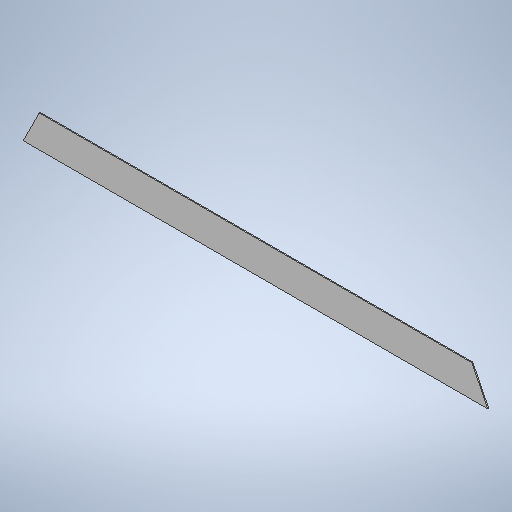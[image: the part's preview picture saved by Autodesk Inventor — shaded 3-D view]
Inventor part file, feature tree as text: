
AUTODESK INVENTOR PART (.ipt)
format: ipt  version: 2025 (Build 290162010, 162A)  size: 272,896 bytes
history: native  units: mm
features: other x2, sheet_metal_op x1, sketch x1
ambient origin geometry x8: Origin, YZ Plane, XZ Plane, XY Plane, X Axis, Y Axis, Z Axis, Center Point
bodies: Solid1 (feature_tree)
feature tree (4):
  sheet_metal_op  "Face1"
  sketch  "Sketch1"  dims[d0=100.0mm d1=1800.0mm d2=3.0mm d3=20.333086mm d6=675.5mm d7=20.333086mm d8=675.5mm]
  other  "Plate1"
  other  "Definition1"
